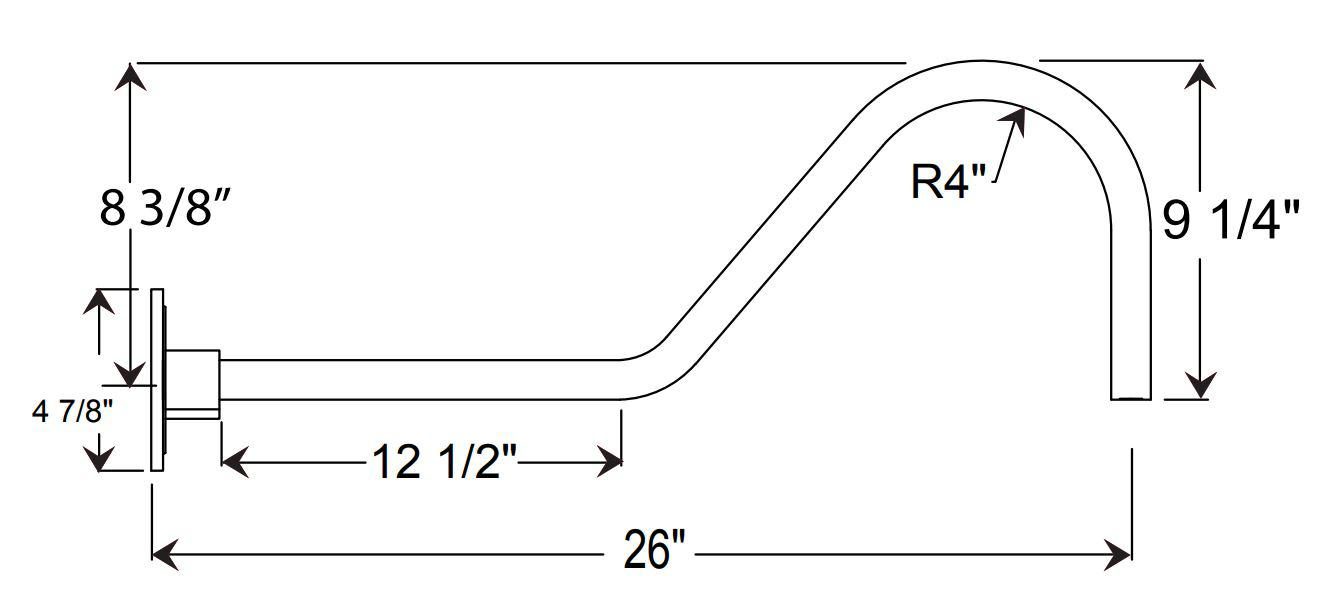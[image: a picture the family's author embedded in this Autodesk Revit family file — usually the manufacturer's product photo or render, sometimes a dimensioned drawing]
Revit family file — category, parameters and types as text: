
# Revit family: SPA- GUP111 MB
name_source: partatom
category: Lighting Fixtures
units: mm (PartAtom-declared; Revit-internal decimal feet)

## family parameters
Always vertical = Yes
Cut with Voids When Loaded = No
Light Source = Yes
OmniClass Number = 23.80.70.00
OmniClass Title = Lighting
Part Type = Normal
Room Calculation Point = No
Round Connector Dimension = Use Diameter
Shared = No
Work Plane-Based = No

## types (1)
- SPA-GUP111
    Apparent Load = 200 VA
    Body Colour = Spun aluminium
    Body Material = body
    CRI = >90
    Color Filter = 16777215
    Construction Material = Heavy Duty spun aluminum.
    Default Elevation = 0' - 0"
    Description = 120-277 Voltage
    Dimming = 1%
    Dimming Lamp Color Temperature Shift = <None>
    Efficiency = 65-125 lumens per watt
    Fixture Diameter = 0' - 6 1/2"
    Fixture Height = 0' - 11 1/2"
    GLASS = Glass
    Lamp = MED-BASE
    Life = L70 50,000 hours
    Load Classification = Lighting
    Manufacturer = ANP Lighting
    Model = SPA-GUP111
    Photometric Web File = generic.ies
    Power Factor = 1
    Ring = RING
    SPA-GUP111 = Yes
    Tilt Angle = 90.00°
    URL = https://www.anplighting.com
    Voltage = 277 V
    Warranty = 5 year limited warranty
    Wattage Comments = 200W Max
    Weight = 1.5 lbs

## geometry (parser evidence)
native form markers: Sweep x23
no freeform markers — native parametric forms only
